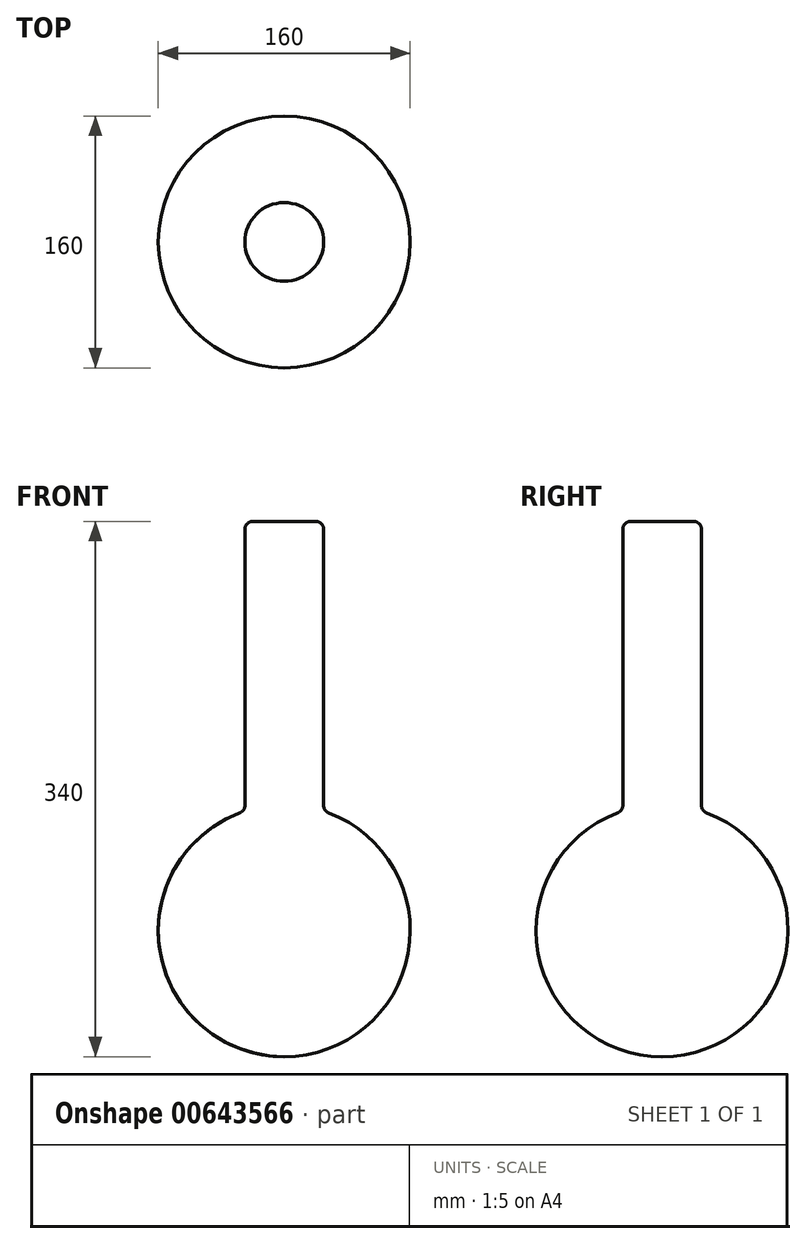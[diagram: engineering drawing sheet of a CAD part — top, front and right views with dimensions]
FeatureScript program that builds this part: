
annotation { "Feature Type Name" : "Feature", "Feature Type Description" : "" }
export const myFeature = defineFeature(function(context is Context, id is Id, definition is map)
    precondition{}
    {
        {
            var Q0;
            Q0=qCreatedBy(makeId("Front.planeOp"),FACE);
            var sketch = newSketch(context, id + "F0", { "sketchPlane" : qUnion([Q0])});
            skCircle(sketch, "E0", {"center": v(0, 0) * mm, "radius": 80 * mm});
            skLineSegment(sketch, "E1", {"start": v(0, 80) * mm, "end": v(0, -80) * mm});
            skSolve(sketch);
        }
        {
            var Q0;
            {var subQ0=sQuery(id+"F0.wireOp",EDGE,"E1");Q0=makeQuery(id+"F0.imprint","IMPRINT",FACE,{"disambiguationData":[TD([[makeQuery(id+"F0.imprint","IMPRINT",EDGE,{"derivedFrom":subQ0}),1.0]])]});}
            var Q1;
            Q1=sQuery(id+"F0.wireOp",EDGE,"E1");
            revolve(context, id + "F1", {"entities" : qUnion([Q0]), "axis" : qUnion([Q1]), "revolveType" : RevolveType.FULL});
        }
        {
            var Q0;
            Q0=qCreatedBy(makeId("Top.planeOp"),FACE);
            var sketch = newSketch(context, id + "F2", { "sketchPlane" : qUnion([Q0])});
            skCircle(sketch, "E2", {"center": v(0, 0) * mm, "radius": 25 * mm});
            skSolve(sketch);
        }
        {
            var Q0;
            Q0 = qSketchRegion(id + "F2", true);
            extrude(context, id + "F3", {"entities" : qUnion([Q0]), "operationType" : NewBodyOperationType.ADD, "depth" : 260 * mm, "offsetDistance" : 25 * mm});
        }
        {
            var Q0;
            Q0=makeQuery(id+"F3.opExtrude","CAP_FACE",FACE,{"disambiguationData":[OSD([sQuery(id+"F2.wireOp",EDGE,"E2")])],"isStart":false});
            fillet(context, id + "F4", {"entities" : qUnion([Q0]), "radius" : 5 * mm, "tangentPropagation" : true, "allowEdgeOverflow" : false});
        }
        {
            var Q0;
            Q0=makeQuery(id+"F3.boolean.opBoolean","INTERSECT",EDGE,{"derivedFrom":[makeQuery(id+"F1.opRevolve","SWEPT_FACE",FACE,{"disambiguationData":[OSD([sQuery(id+"F0.wireOp",EDGE,"E0")])]}),makeQuery(id+"F3.opExtrude","SWEPT_FACE",FACE,{"disambiguationData":[OSD([sQuery(id+"F2.wireOp",EDGE,"E2")])]})]});
            fillet(context, id + "F5", {"entities" : qUnion([Q0]), "radius" : 5 * mm, "tangentPropagation" : true, "allowEdgeOverflow" : false});
        }
    });
